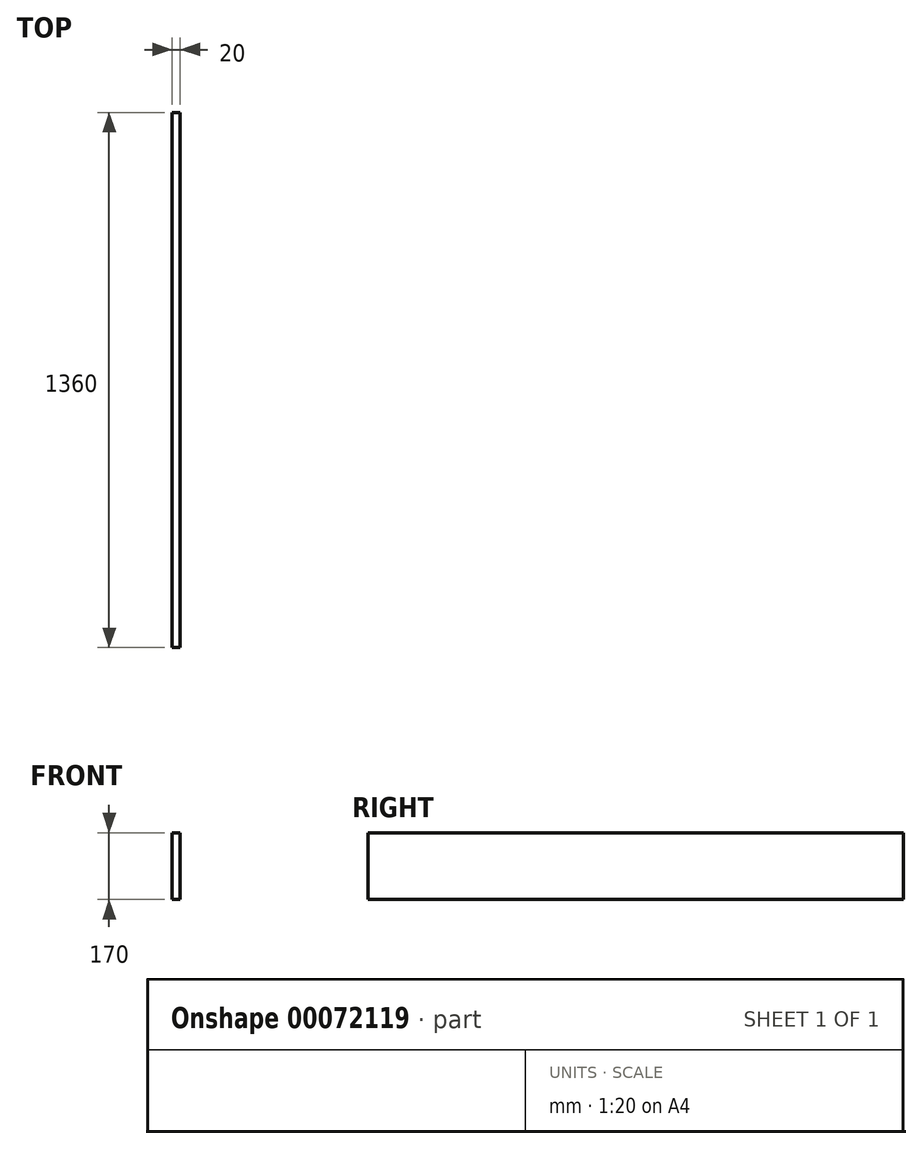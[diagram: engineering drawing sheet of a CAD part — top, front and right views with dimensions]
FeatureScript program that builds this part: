
annotation { "Feature Type Name" : "Feature", "Feature Type Description" : "" }
export const myFeature = defineFeature(function(context is Context, id is Id, definition is map)
    precondition{}
    {
        {
            var Q0;
            Q0=qCreatedBy(makeId("Top.planeOp"),FACE);
            var sketch = newSketch(context, id + "F0", { "sketchPlane" : qUnion([Q0])});
            skLineSegment(sketch, "E0.bottom", {"start": v(-68.73, 213.92) * mm, "end": v(1291.27, 213.92) * mm});
            skLineSegment(sketch, "E0.top", {"start": v(-68.73, 43.92) * mm, "end": v(1291.27, 43.92) * mm});
            skLineSegment(sketch, "E0.left", {"start": v(-68.73, 213.92) * mm, "end": v(-68.73, 43.92) * mm});
            skLineSegment(sketch, "E0.right", {"start": v(1291.27, 213.92) * mm, "end": v(1291.27, 43.92) * mm});
            skSolve(sketch);
        }
        {
            var Q0;
            Q0 = qSketchRegion(id + "F0", true);
            extrude(context, id + "F1", {"entities" : qUnion([Q0]), "depth" : 20 * mm});
        }
        {
            var Q0;
            Q0=makeQuery(id+"F1.opExtrude","SWEPT_BODY",BODY,{"disambiguationData":[OSD([sQuery(id+"F0.wireOp",EDGE,"E0.bottom"),sQuery(id+"F0.wireOp",EDGE,"E0.top"),sQuery(id+"F0.wireOp",EDGE,"E0.left"),sQuery(id+"F0.wireOp",EDGE,"E0.right")])]});
            var Q1;
            Q1=makeQuery(id+"F1.opExtrude","SWEPT_EDGE",EDGE,{"disambiguationData":[OSD([sQuery(id+"F0.wireOp",EDGE,"E0.top"),sQuery(id+"F0.wireOp",EDGE,"E0.left")])]});
            transform(context, id + "F2", {"entities" : qUnion([Q0]), "transformType" : TransformType.ROTATION, "transformAxis" : qUnion([Q1]), "angle" : 90 * degree, "makeCopy" : false});
        }
        {
            var Q0;
            Q0=makeQuery(id+"F1.opExtrude","SWEPT_BODY",BODY,{"disambiguationData":[OSD([sQuery(id+"F0.wireOp",EDGE,"E0.bottom"),sQuery(id+"F0.wireOp",EDGE,"E0.top"),sQuery(id+"F0.wireOp",EDGE,"E0.left"),sQuery(id+"F0.wireOp",EDGE,"E0.right")])]});
            var Q1;
            Q1=makeQuery(id+"F1.opExtrude","CAP_EDGE",EDGE,{"disambiguationData":[OSD([sQuery(id+"F0.wireOp",EDGE,"E0.top")])],"isStart":false});
            transform(context, id + "F3", {"entities" : qUnion([Q0]), "transformType" : TransformType.ROTATION, "transformAxis" : qUnion([Q1]), "angle" : 90 * degree, "makeCopy" : false});
        }
    });
